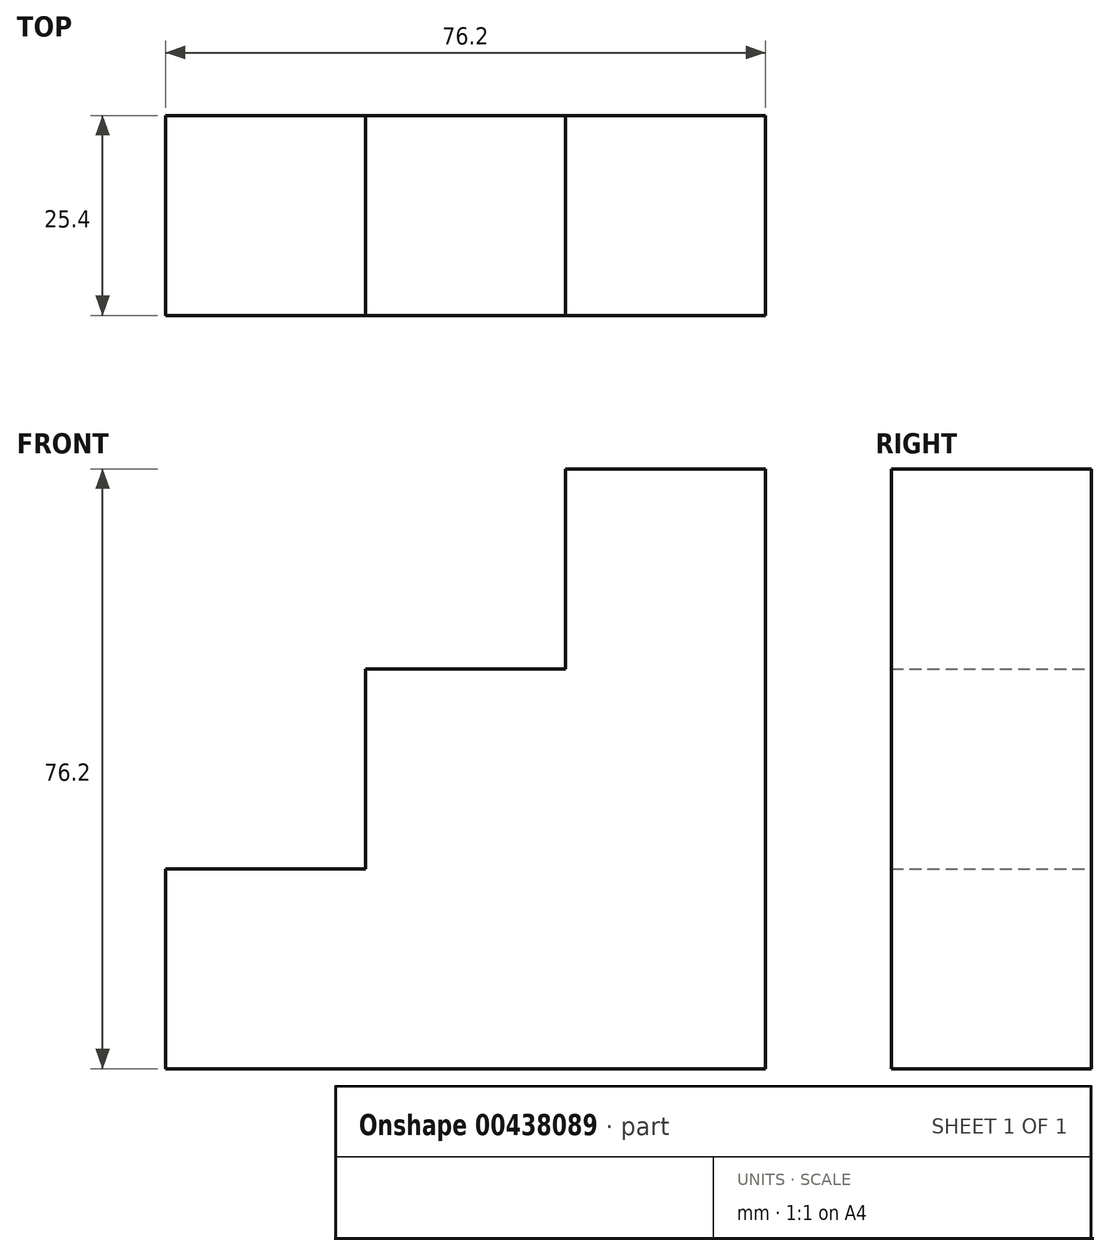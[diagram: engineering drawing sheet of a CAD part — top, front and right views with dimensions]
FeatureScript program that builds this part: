
annotation { "Feature Type Name" : "Feature", "Feature Type Description" : "" }
export const myFeature = defineFeature(function(context is Context, id is Id, definition is map)
    precondition{}
    {
        {
            var Q0;
            Q0=qCreatedBy(makeId("Front.planeOp"),FACE);
            var sketch = newSketch(context, id + "F0", { "sketchPlane" : qUnion([Q0])});
            skLineSegment(sketch, "E0", {"start": v(35.88, 60.54) * mm, "end": v(10.48, 60.54) * mm});
            skLineSegment(sketch, "E1", {"start": v(10.48, 60.54) * mm, "end": v(10.48, 35.14) * mm});
            skLineSegment(sketch, "E2", {"start": v(10.48, 35.14) * mm, "end": v(-14.92, 35.14) * mm});
            skLineSegment(sketch, "E3", {"start": v(-14.92, 35.14) * mm, "end": v(-14.92, 9.74) * mm});
            skLineSegment(sketch, "E4", {"start": v(-14.92, 9.74) * mm, "end": v(-40.32, 9.74) * mm});
            skLineSegment(sketch, "E5", {"start": v(-40.32, 9.74) * mm, "end": v(-40.32, -15.66) * mm});
            skLineSegment(sketch, "E6", {"start": v(-40.32, -15.66) * mm, "end": v(35.88, -15.66) * mm});
            skLineSegment(sketch, "E7", {"start": v(35.88, -15.66) * mm, "end": v(35.88, 60.54) * mm});
            skSolve(sketch);
        }
        {
            var Q0;
            Q0=makeQuery(id+"F0.imprint","IMPRINT",FACE,{"disambiguationData":[TD([[makeQuery(id+"F0.imprint","IMPRINT",EDGE,{"derivedFrom":sQuery(id+"F0.wireOp",EDGE,"E0")}),1.0]])]});
            extrude(context, id + "F1", {"entities" : qUnion([Q0]), "depth" : 25.4 * mm});
        }
    });
